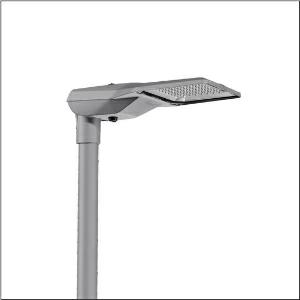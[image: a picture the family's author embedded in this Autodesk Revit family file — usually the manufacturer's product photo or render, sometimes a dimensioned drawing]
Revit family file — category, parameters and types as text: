
# Revit family: streetlight_sl_21_iq_midi___st1_0a_5xe3d31y08mb_3ca9
name_source: partatom
category: Lighting Fixtures
units: mm (PartAtom-declared; Revit-internal decimal feet)

## family parameters
Cut with Voids When Loaded = No
Host = Face
Light Source = No
Part Type = Normal
Room Calculation Point = No
Round Connector Dimension = Use Diameter
Shared = No

## types (1)
- --- (1 x LED, 18340 lm, 129.3 W, 3000K)
    Apparent Load = 129 VA
    CIE Flux Codes = 37 72 97 100 100
    Color Rendering = 70
    Color Temperature = 3000K
    Default Elevation = 1800 mm
    Description = Streetlight SL 21 iQ midi, mast luminaire, primary light control with lens, of PMMA, primary optical cover: cover, of toughened safety glass, transparent, light distribution: ST1.0a, light emission: direct distribution, primary light characteristic: asymmetric, installation type: post-top, side-entry, LED, High Power LED, rated luminous flux: 18.340lm, luminous efficacy: 142lm/W, light colour: 730, colour temperature: 3000K, control: presetting dimming logarithmic, Street-Remote, Auto-Match, Temp-Guard, Lumen-Switch, Night-Set, Smart-Wire, Light-Fading, Desk-Remote (wireless, voltage-free reading and setting of iQ features in the workshop via application-optimized NFC function/RFID function), optimised constant luminous flux control (CLO 2.0), mains connection: 230..240V, AC, 50/60Hz, start of lifetime: 129W, end of service life: 142W, reduction: 56W, luminaire housing, of diecast aluminium, powder-coated, Siteco® metallic grey (DB 702S), corrosivity category C5 mid according to DIN EN ISO 12944, please order mast flange separately, inclination adjustable: 0°, 5°, 10°, 15°, sealing non-destructively replaceable, multi-level sealing system, length: 644mm, width: 335mm, height: 110mm, mast flange for spigot size: 42mm (side-entry): 5XC10008XM4, 60/48mm (side-entry/post-top): 5XC10108XM2, 76/60mm (side-entry/post-top): 5XC10108XM1, Smart Interface below and above, protection rating (complete): IP66, insulation class (complete): insulation class II (safety insulation), certification: CE, ENEC, ENEC+, VDE, impact resistance: IK09, permissible operating ambient temperature for outdoor applications: -40..+50°C, standard-compliant lighting for roads and squares, packaging unit: 1 piece

Light Distribution: ST1.0a
    Height = 111 mm
    Lamp = 1 x LED
    Lamp Light Flux = 18340 lm
    Lamp Power = 129.3 W
    Lamp count = 1
    Length = 644 mm
    Luminous efficacy = 142 lm/W
    Manufacturer = Siteco
    ModVariant = No
    Model = 5XE3D31Y08MB
    Number of Poles = 1
    OnlyDefault = Yes
    Power Factor = 1
    Product Name = Streetlight SL 21 iQ midi | ST1.0a
    Product group = mast luminaire | pylon top
    ProductGroupID = 6100
    Protection Class = Protection class II
    Protection Degree = IP 66
    RLX_Detail_Level = 1
    RLX_Emergency_Light_Flux = 0 lm
    RLX_Emergency_Type = 0
    RLX_Emergency_Type_DB = No
    RlxData = <blob elided: 91369 chars, md5=34ecb06e>
    Socket = socket
    Standby Power = 0 W
    System Light Flux = 18340 lm
    System Power = 129 W
    Type Comments = factory setting: luminous flux: 100 % | dim-lin: 254 | 672 mA
    Type Image = l_1004304.jpg
    URL = http://relux.com
    VarID = @adj_044569
    Voltage = 0 V
    Weight = 0.00 kg
    Width = 336 mm

## geometry (parser evidence)
native form markers: Blend x4, Sweep x11
no freeform markers — native parametric forms only
